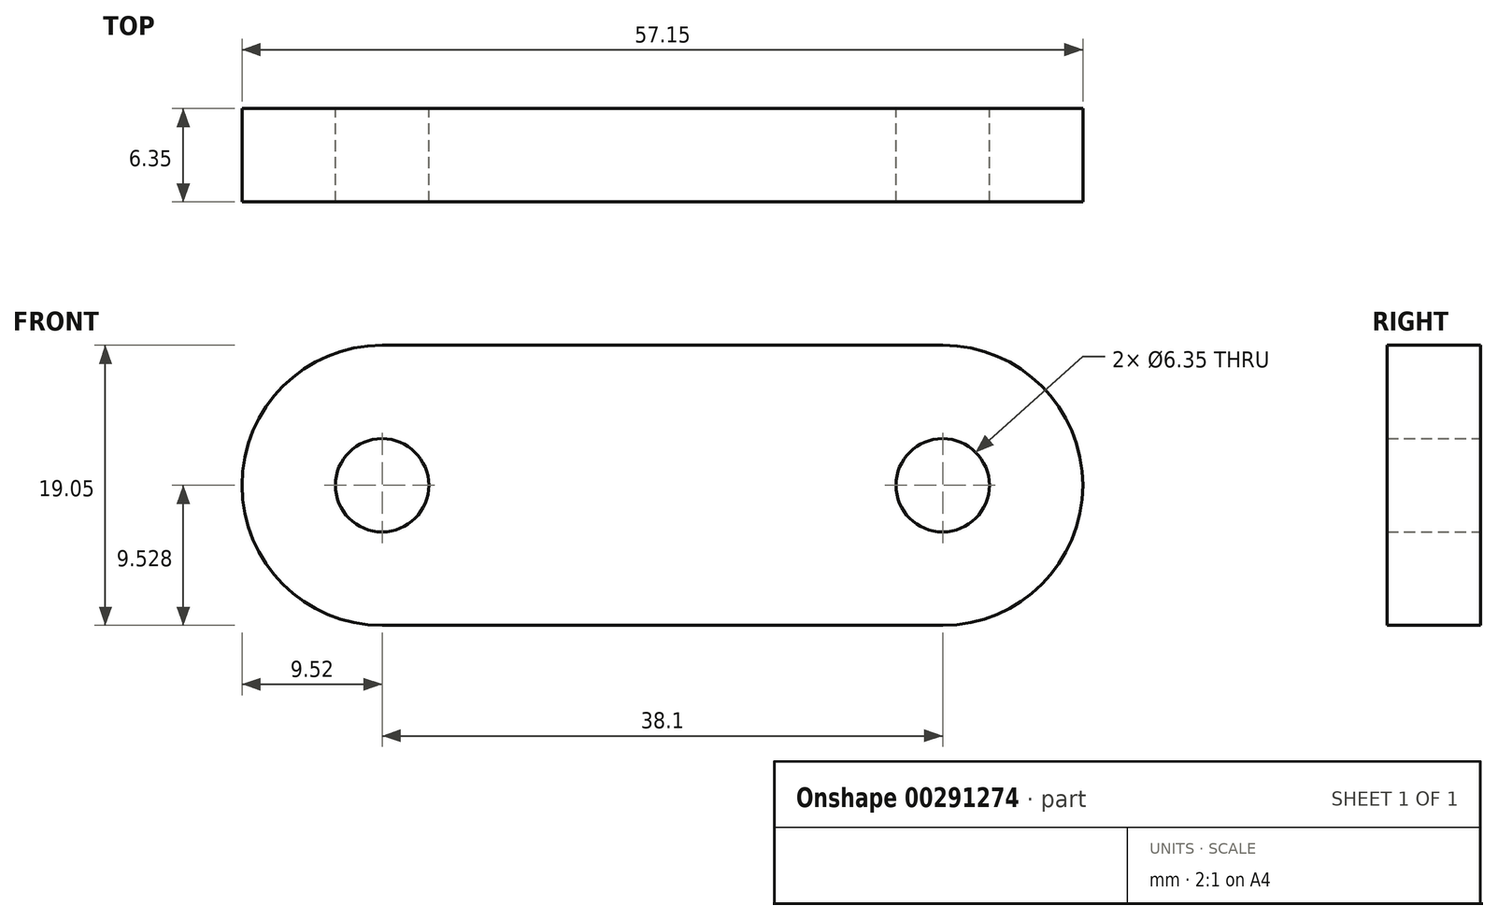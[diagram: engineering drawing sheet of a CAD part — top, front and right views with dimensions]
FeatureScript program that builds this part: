
annotation { "Feature Type Name" : "Feature", "Feature Type Description" : "" }
export const myFeature = defineFeature(function(context is Context, id is Id, definition is map)
    precondition{}
    {
        {
            var Q0;
            Q0=qCreatedBy(makeId("Front.planeOp"),FACE);
            var sketch = newSketch(context, id + "F0", { "sketchPlane" : qUnion([Q0])});
            skLineSegment(sketch, "E0.bottom", {"start": v(-38.1, 39.2) * mm, "end": v(0, 39.2) * mm});
            skLineSegment(sketch, "E0.top", {"start": v(-38.1, 20.15) * mm, "end": v(0, 20.15) * mm});
            skArc(sketch, "E1", {"start": v(0, 20.15) * mm, "mid": v(9.52, 29.68) * mm, "end": v(0, 39.2) * mm});
            skArc(sketch, "E2", {"start": v(-38.1, 39.2) * mm, "mid": v(-47.62, 29.68) * mm, "end": v(-38.1, 20.15) * mm});
            skCircle(sketch, "E3", {"center": v(-38.1, 29.68) * mm, "radius": 3.18 * mm});
            skCircle(sketch, "E4", {"center": v(0, 29.68) * mm, "radius": 3.18 * mm});
            skSolve(sketch);
        }
        {
            var Q0;
            Q0=makeQuery(id+"F0.imprint","IMPRINT",FACE,{"disambiguationData":[TD([[makeQuery(id+"F0.imprint","IMPRINT",EDGE,{"derivedFrom":sQuery(id+"F0.wireOp",EDGE,"E0.bottom")}),-1.0]])]});
            extrude(context, id + "F1", {"entities" : qUnion([Q0]), "depth" : 6.35 * mm});
        }
    });
